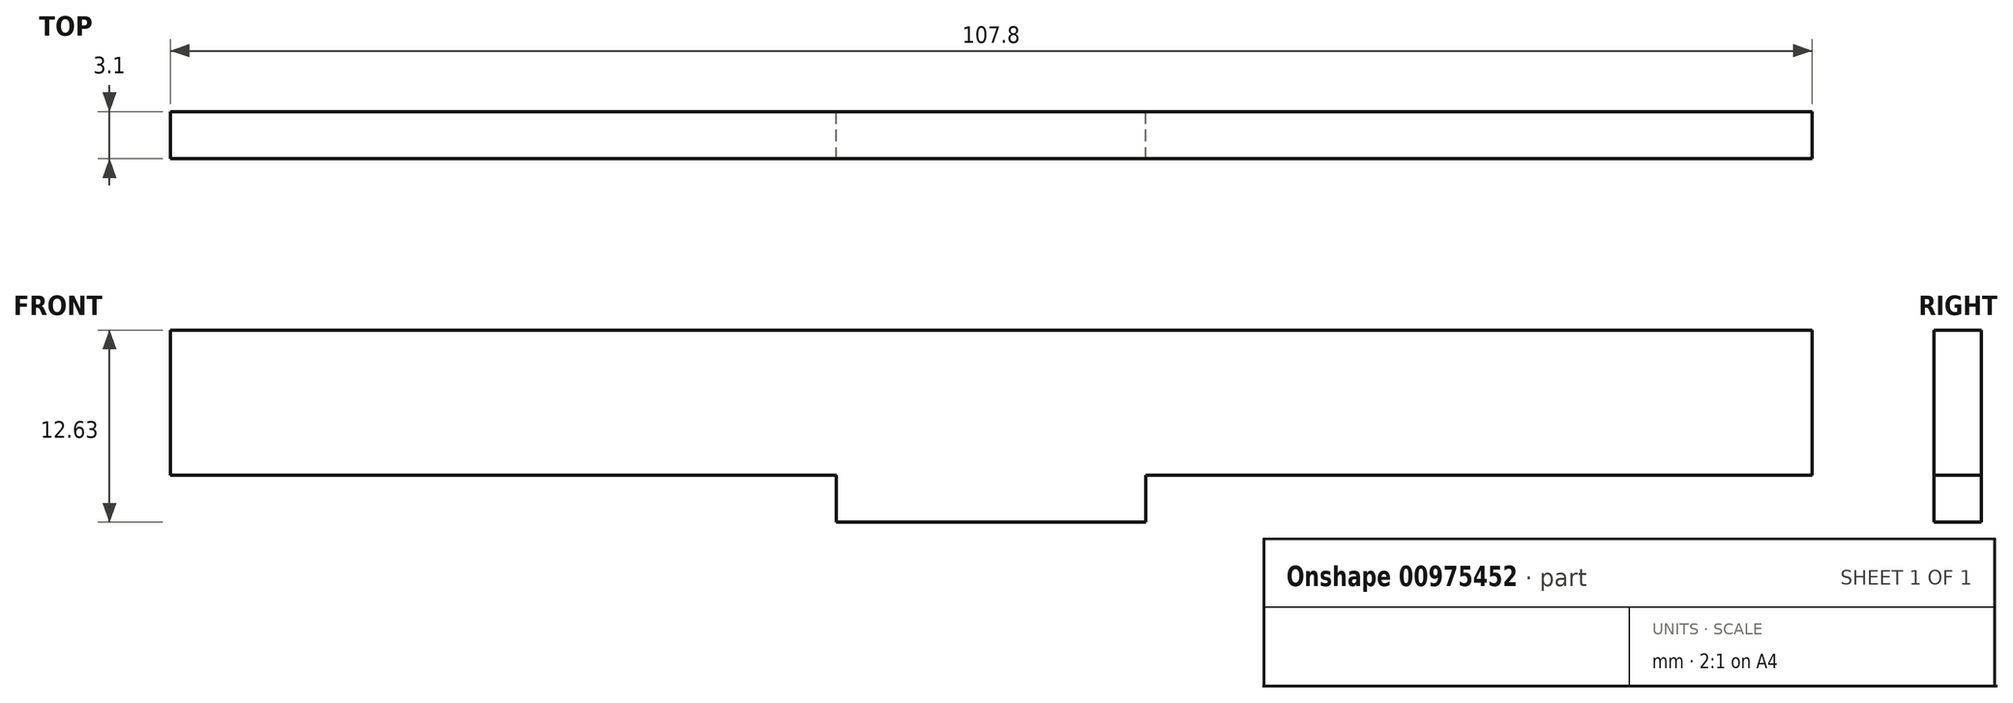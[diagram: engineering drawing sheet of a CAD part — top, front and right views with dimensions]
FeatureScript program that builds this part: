
annotation { "Feature Type Name" : "Feature", "Feature Type Description" : "" }
export const myFeature = defineFeature(function(context is Context, id is Id, definition is map)
    precondition{}
    {
        {
            var Q0;
            Q0=qCreatedBy(makeId("Front.planeOp"),FACE);
            var sketch = newSketch(context, id + "F0", { "sketchPlane" : qUnion([Q0])});
            skLineSegment(sketch, "E0.bottom", {"start": v(0, 0) * mm, "end": v(107.8, 0) * mm});
            skLineSegment(sketch, "E0.top", {"start": v(0, 9.52) * mm, "end": v(107.8, 9.52) * mm});
            skLineSegment(sketch, "E0.left", {"start": v(0, 0) * mm, "end": v(0, 9.52) * mm});
            skLineSegment(sketch, "E0.right", {"start": v(107.8, 0) * mm, "end": v(107.8, 9.52) * mm});
            skLineSegment(sketch, "E1.bottom", {"start": v(43.74, 0) * mm, "end": v(64.06, 0) * mm});
            skLineSegment(sketch, "E1.top", {"start": v(43.74, -3.1) * mm, "end": v(64.06, -3.1) * mm});
            skLineSegment(sketch, "E1.left", {"start": v(43.74, 0) * mm, "end": v(43.74, -3.1) * mm});
            skLineSegment(sketch, "E1.right", {"start": v(64.06, 0) * mm, "end": v(64.06, -3.1) * mm});
            skLineSegment(sketch, "E2", {"start": v(53.9, 9.52) * mm, "end": v(53.9, 0) * mm, "construction": true});
            skLineSegment(sketch, "E3", {"start": v(53.9, 0) * mm, "end": v(53.9, 3.07) * mm});
            skSolve(sketch);
        }
        {
            var Q0;
            Q0=makeQuery(id+"F0.imprint","IMPRINT",FACE,{"disambiguationData":[TD([[makeQuery(id+"F0.imprint","IMPRINT",EDGE,{"derivedFrom":sQuery(id+"F0.wireOp",EDGE,"E0.top")}),-1.0]])]});
            var Q1;
            Q1=makeQuery(id+"F0.imprint","IMPRINT",FACE,{"disambiguationData":[TD([[makeQuery(id+"F0.imprint","IMPRINT",EDGE,{"derivedFrom":sQuery(id+"F0.wireOp",EDGE,"E1.top")}),1.0]])]});
            extrude(context, id + "F1", {"entities" : qUnion([Q0, Q1]), "depth" : 3.1 * mm, "offsetDistance" : 25.4 * mm});
        }
    });
